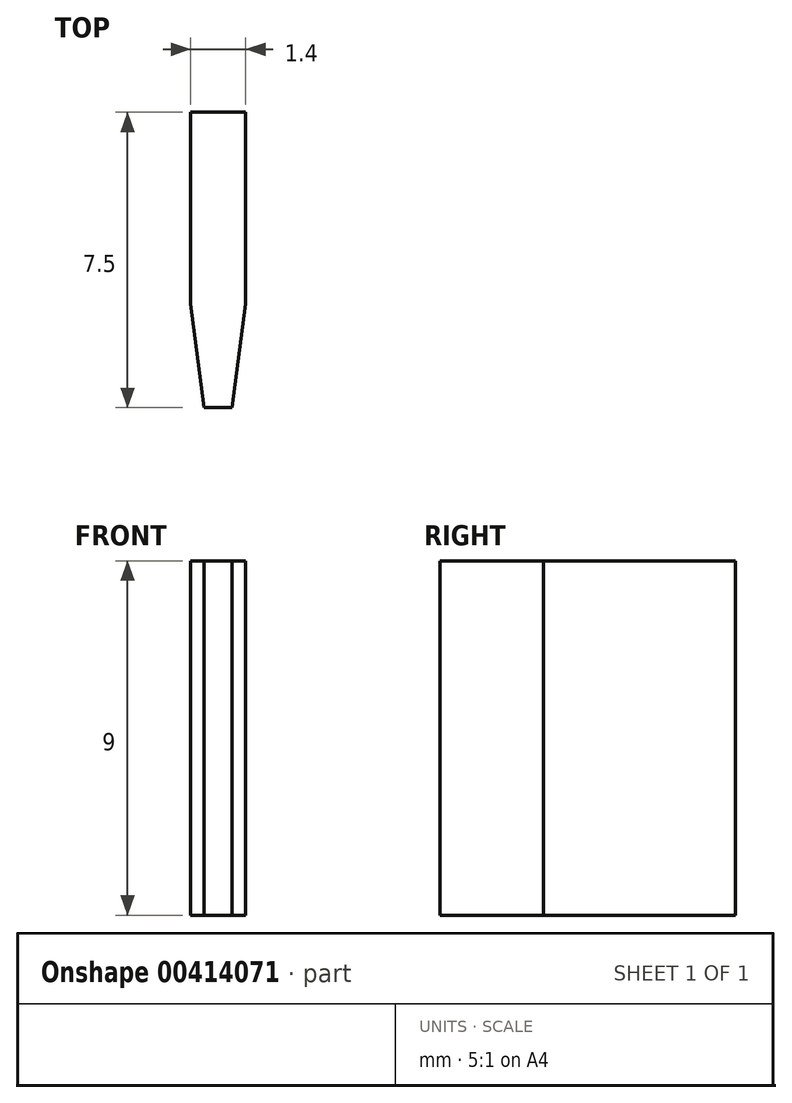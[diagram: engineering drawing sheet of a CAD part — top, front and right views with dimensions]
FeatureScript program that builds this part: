
annotation { "Feature Type Name" : "Feature", "Feature Type Description" : "" }
export const myFeature = defineFeature(function(context is Context, id is Id, definition is map)
    precondition{}
    {
        {
            var Q0;
            Q0=qCreatedBy(makeId("Front.planeOp"),FACE);
            var sketch = newSketch(context, id + "F0", { "sketchPlane" : qUnion([Q0])});
            skLineSegment(sketch, "E0.bottom", {"start": v(0, 0) * mm, "end": v(1.4, 0) * mm});
            skLineSegment(sketch, "E0.top", {"start": v(0, -9) * mm, "end": v(1.4, -9) * mm});
            skLineSegment(sketch, "E0.left", {"start": v(0, 0) * mm, "end": v(0, -9) * mm});
            skLineSegment(sketch, "E0.right", {"start": v(1.4, 0) * mm, "end": v(1.4, -9) * mm});
            skSolve(sketch);
        }
        {
            var Q0;
            Q0=makeQuery(id+"F0.imprint","IMPRINT",FACE,{"disambiguationData":[TD([[makeQuery(id+"F0.imprint","IMPRINT",EDGE,{"derivedFrom":sQuery(id+"F0.wireOp",EDGE,"E0.bottom")}),-1.0]])]});
            extrude(context, id + "F1", {"entities" : qUnion([Q0]), "depth" : 7.5 * mm});
        }
        {
            var Q0;
            Q0=makeQuery(id+"F1.opExtrude","SWEPT_FACE",FACE,{"disambiguationData":[OSD([sQuery(id+"F0.wireOp",EDGE,"E0.bottom")])]});
            var sketch = newSketch(context, id + "F2", { "sketchPlane" : qUnion([Q0])});
            skLineSegment(sketch, "E1", {"start": v(0.7, -7.5) * mm, "end": v(0.7, 0) * mm});
            skPoint(sketch, "E2", {"position": v(0.7, -7.5) * mm});
            skLineSegment(sketch, "E3", {"start": v(0.7, -7.5) * mm, "end": v(0, -7.5) * mm});
            skLineSegment(sketch, "E4", {"start": v(0.7, -7.5) * mm, "end": v(1.4, -7.5) * mm});
            skPoint(sketch, "E5", {"position": v(1.05, -7.5) * mm});
            skPoint(sketch, "E6", {"position": v(0.35, -7.5) * mm});
            skLineSegment(sketch, "E7", {"start": v(0.35, -7.5) * mm, "end": v(0, -4.87) * mm});
            skLineSegment(sketch, "E8", {"start": v(0, -4.87) * mm, "end": v(1.4, -4.87) * mm});
            skLineSegment(sketch, "E9", {"start": v(1.4, -4.87) * mm, "end": v(1.05, -7.5) * mm});
            skSolve(sketch);
        }
        {
            var Q0;
            {var subQ3=sQuery(id+"F2.wireOp",EDGE,"E7");Q0=makeQuery(id+"F2.imprint","IMPRINT",FACE,{"disambiguationData":[TD([[makeQuery(id+"F2.imprint","IMPRINT",EDGE,{"derivedFrom":subQ3}),1.0]])]});}
            var Q1;
            {var subQ3=sQuery(id+"F2.wireOp",EDGE,"E9");Q1=makeQuery(id+"F2.imprint","IMPRINT",FACE,{"disambiguationData":[TD([[makeQuery(id+"F2.imprint","IMPRINT",EDGE,{"derivedFrom":subQ3}),1.0]])]});}
            extrude(context, id + "F3", {"entities" : qUnion([Q0, Q1]), "operationType" : NewBodyOperationType.REMOVE, "oppositeDirection" : true, "depth" : 25.4 * mm});
        }
    });
